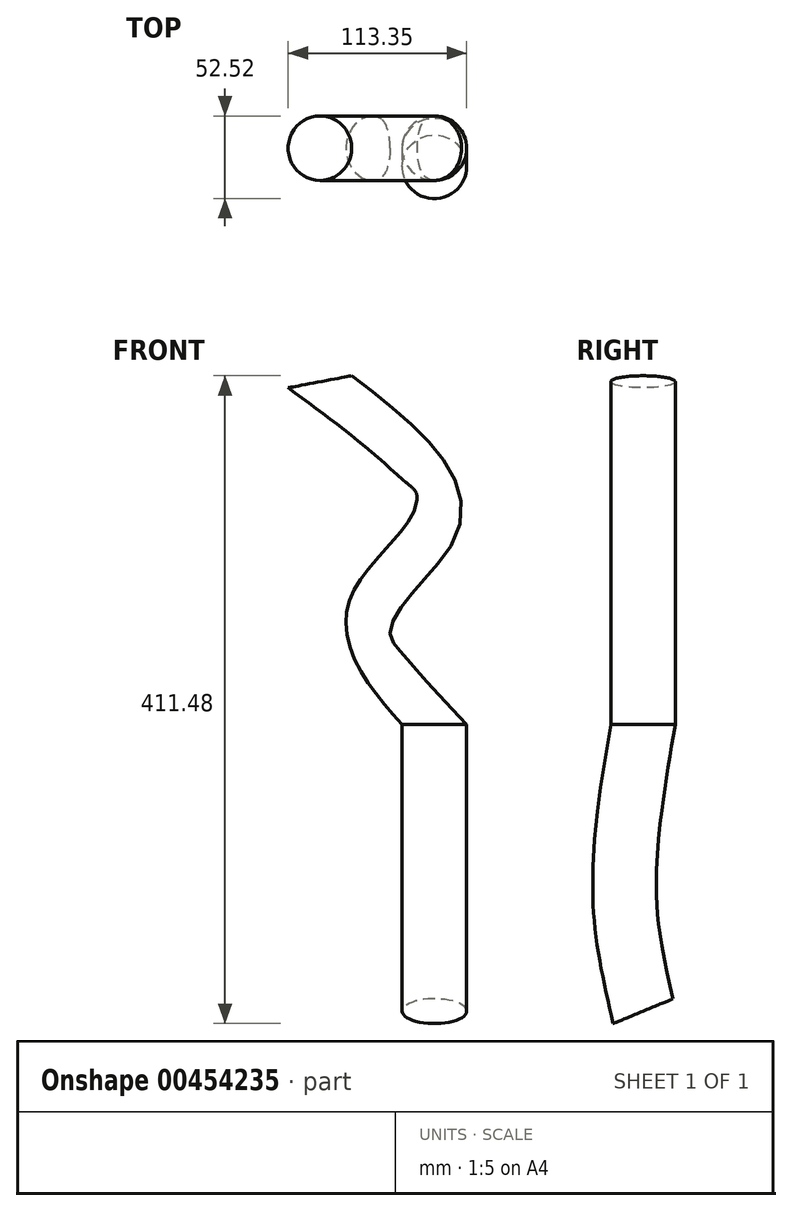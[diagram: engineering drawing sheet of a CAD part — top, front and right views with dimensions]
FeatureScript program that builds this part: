
annotation { "Feature Type Name" : "Feature", "Feature Type Description" : "" }
export const myFeature = defineFeature(function(context is Context, id is Id, definition is map)
    precondition{}
    {
        {
            var Q0;
            Q0=qCreatedBy(makeId("Top.planeOp"),FACE);
            var sketch = newSketch(context, id + "F0", { "sketchPlane" : qUnion([Q0])});
            skCircle(sketch, "E0", {"center": v(0, 0) * mm, "radius": 20.5 * mm});
            skSolve(sketch);
        }
        {
            var Q0;
            Q0=qCreatedBy(makeId("Right.planeOp"),FACE);
            var sketch = newSketch(context, id + "F1", { "sketchPlane" : qUnion([Q0])});
            skFitSpline(sketch, "E1", {"points": [v(0, 0) * mm, v(-11.72, -106.56) * mm, v(0, -182.13) * mm], "startDerivative": vector(-34.42, -205.1) * mm, "endDerivative": vector(36.4, -157.82) * mm});
            skSolve(sketch);
        }
        {
            var Q0;
            Q0=makeQuery(id+"F0.imprint","IMPRINT",FACE,{"disambiguationData":[TD([[makeQuery(id+"F0.imprint","IMPRINT",EDGE,{"derivedFrom":sQuery(id+"F0.wireOp",EDGE,"E0")}),1.0]])]});
            var Q1;
            Q1=sQuery(id+"F1.wireOp",EDGE,"E1");
            sweep(context, id + "F2", {"profiles" : qUnion([Q0]), "path" : qUnion([Q1])});
        }
        {
            var Q0;
            Q0=qCreatedBy(makeId("Front.planeOp"),FACE);
            var sketch = newSketch(context, id + "F3", { "sketchPlane" : qUnion([Q0])});
            skFitSpline(sketch, "E2", {"points": [v(0, 0) * mm, v(-38.44, 70.5) * mm, v(0, 134.15) * mm, v(-72.7, 217.7) * mm], "startDerivative": vector(-206.3, 225.8) * mm, "endDerivative": vector(-304.65, 228.7) * mm});
            skSolve(sketch);
        }
        {
            var Q0;
            Q0=makeQuery(id+"F2.opSweep","CAP_FACE",FACE,{"disambiguationData":[OSD([sQuery(id+"F0.wireOp",EDGE,"E0"),sQuery(id+"F1.wireOp",VERTEX,"E1.start")])],"isStart":true});
            var Q1;
            Q1=sQuery(id+"F3.wireOp",EDGE,"E2");
            sweep(context, id + "F4", {"operationType" : NewBodyOperationType.ADD, "profiles" : qUnion([Q0]), "path" : qUnion([Q1])});
        }
    });
